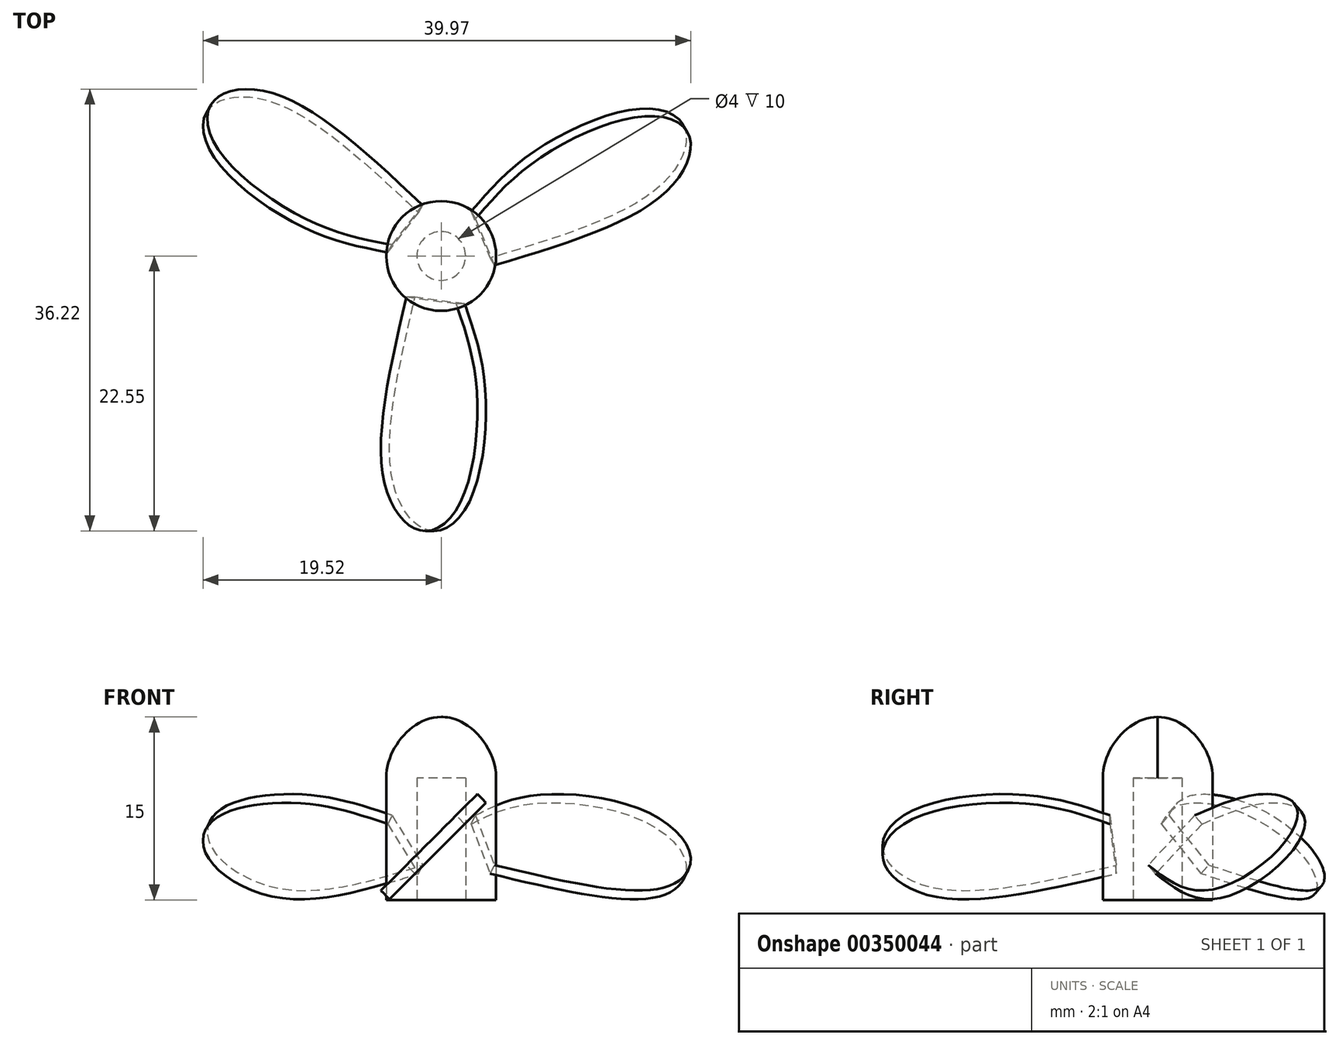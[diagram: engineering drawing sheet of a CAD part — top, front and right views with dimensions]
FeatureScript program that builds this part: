
annotation { "Feature Type Name" : "Feature", "Feature Type Description" : "" }
export const myFeature = defineFeature(function(context is Context, id is Id, definition is map)
    precondition{}
    {
        {
            var Q0;
            Q0=qCreatedBy(makeId("Top.planeOp"),FACE);
            var sketch = newSketch(context, id + "F0", { "sketchPlane" : qUnion([Q0])});
            skCircle(sketch, "E0", {"center": v(0, 0) * mm, "radius": 20 * mm, "construction": true});
            skCircle(sketch, "E1", {"center": v(0, 0) * mm, "radius": 4.5 * mm});
            skCircle(sketch, "E2", {"center": v(0, 0) * mm, "radius": 2 * mm});
            skSolve(sketch);
        }
        {
            var Q0;
            Q0=qSketchRegion(id+"F0",true);
            extrude(context, id + "F1", {"entities" : qUnion([Q0]), "depth" : 10 * mm});
        }
        {
            var Q0;
            Q0=qCreatedBy(makeId("Front.planeOp"),FACE);
            var sketch = newSketch(context, id + "F2", { "sketchPlane" : qUnion([Q0])});
            skLineSegment(sketch, "E3", {"start": v(0, 15) * mm, "end": v(0, 10) * mm});
            skLineSegment(sketch, "E4", {"start": v(0, 10) * mm, "end": v(4.5, 10) * mm});
            skFitSpline(sketch, "E5", {"points": [v(0, 15) * mm, v(1.82, 14.5) * mm, v(4.5, 10) * mm], "startDerivative": vector(3.13, 0) * mm, "endDerivative": vector(0, -10.08) * mm});
            skSolve(sketch);
        }
        {
            var Q0;
            Q0=makeQuery(id+"F2.imprint","IMPRINT",FACE,{"disambiguationData":[TD([[makeQuery(id+"F2.imprint","IMPRINT",EDGE,{"derivedFrom":sQuery(id+"F2.wireOp",EDGE,"E3")}),1.0]])]});
            var Q1;
            Q1=sQuery(id+"F2.wireOp",EDGE,"E3");
            revolve(context, id + "F3", {"operationType" : NewBodyOperationType.ADD, "entities" : qUnion([Q0]), "axis" : qUnion([Q1]), "revolveType" : RevolveType.FULL});
        }
        {
            var Q0;
            Q0=qCreatedBy(makeId("Front.planeOp"),FACE);
            var sketch = newSketch(context, id + "F4", { "sketchPlane" : qUnion([Q0])});
            skLineSegment(sketch, "E6", {"start": v(-4.2, 9.2) * mm, "end": v(4.2, 0.8) * mm, "construction": true});
            skLineSegment(sketch, "E7", {"start": v(0, 5) * mm, "end": v(0, 0) * mm, "construction": true});
            skSolve(sketch);
        }
        {
            var Q0;
            Q0=sQuery(id+"F4.wireOp",EDGE,"E6");
            cPoint(context, id + "F5", {"entities" : qUnion([Q0]), "parameter" : 0.5});
        }
        {
            var Q0;
            Q0=sQuery(id+"F4.wireOp",EDGE,"E6");
            var Q1;
            Q1=qCreatedBy(id+"F5",VERTEX);
            cPlane(context, id + "F6", {"entities" : qUnion([Q0, Q1]), "cplaneType" : CPlaneType.LINE_POINT, "offset" : 25 * mm, "width" : 150 * mm, "height" : 150 * mm});
        }
        {
            var Q0;
            Q0=qCreatedBy(id+"F6.planeOp",FACE);
            var sketch = newSketch(context, id + "F7", { "sketchPlane" : qUnion([Q0])});
            skFitSpline(sketch, "E8", {"points": [v(-3.93, 5.76) * mm, v(-10.75, 8.12) * mm, v(-20.14, 6.3) * mm, v(-22.5, 1.58) * mm, v(-18.18, -2.68) * mm, v(-3.4, 0) * mm], "startDerivative": vector(-33.23, 16.46) * mm, "endDerivative": vector(61.66, 20.48) * mm});
            skLineSegment(sketch, "E9", {"start": v(-3.93, 5.76) * mm, "end": v(-3.4, 0) * mm});
            skSolve(sketch);
        }
        {
            var Q0;
            Q0=makeQuery(id+"F7.imprint","IMPRINT",FACE,{"disambiguationData":[TD([[makeQuery(id+"F7.imprint","IMPRINT",EDGE,{"derivedFrom":sQuery(id+"F7.wireOp",EDGE,"E8")}),1.0]])]});
            extrude(context, id + "F8", {"entities" : qUnion([Q0]), "depth" : 0.5 * mm, "hasSecondDirection" : true, "secondDirectionOppositeDirection" : true, "secondDirectionDepth" : 0.5 * mm});
        }
        {
            var Q0;
            Q0=qCreatedBy(makeId("Front.planeOp"),FACE);
            var sketch = newSketch(context, id + "F9", { "sketchPlane" : qUnion([Q0])});
            skLineSegment(sketch, "E10", {"start": v(0, 0) * mm, "end": v(0, 8.52) * mm, "construction": true});
            skSolve(sketch);
        }
        {
            var Q0;
            Q0=makeQuery(id+"F8.opExtrude","SWEPT_BODY",BODY,{"disambiguationData":[OSD([sQuery(id+"F7.wireOp",EDGE,"E8"),sQuery(id+"F7.wireOp",EDGE,"E9")])]});
            var Q1;
            Q1=sQuery(id+"F9.wireOp",EDGE,"E10");
            circularPattern(context, id + "F10", {"entities" : qUnion([Q0]), "axis" : qUnion([Q1]), "angle" : 360 * degree, "instanceCount" : 3, "equalSpace" : true});
        }
    });
